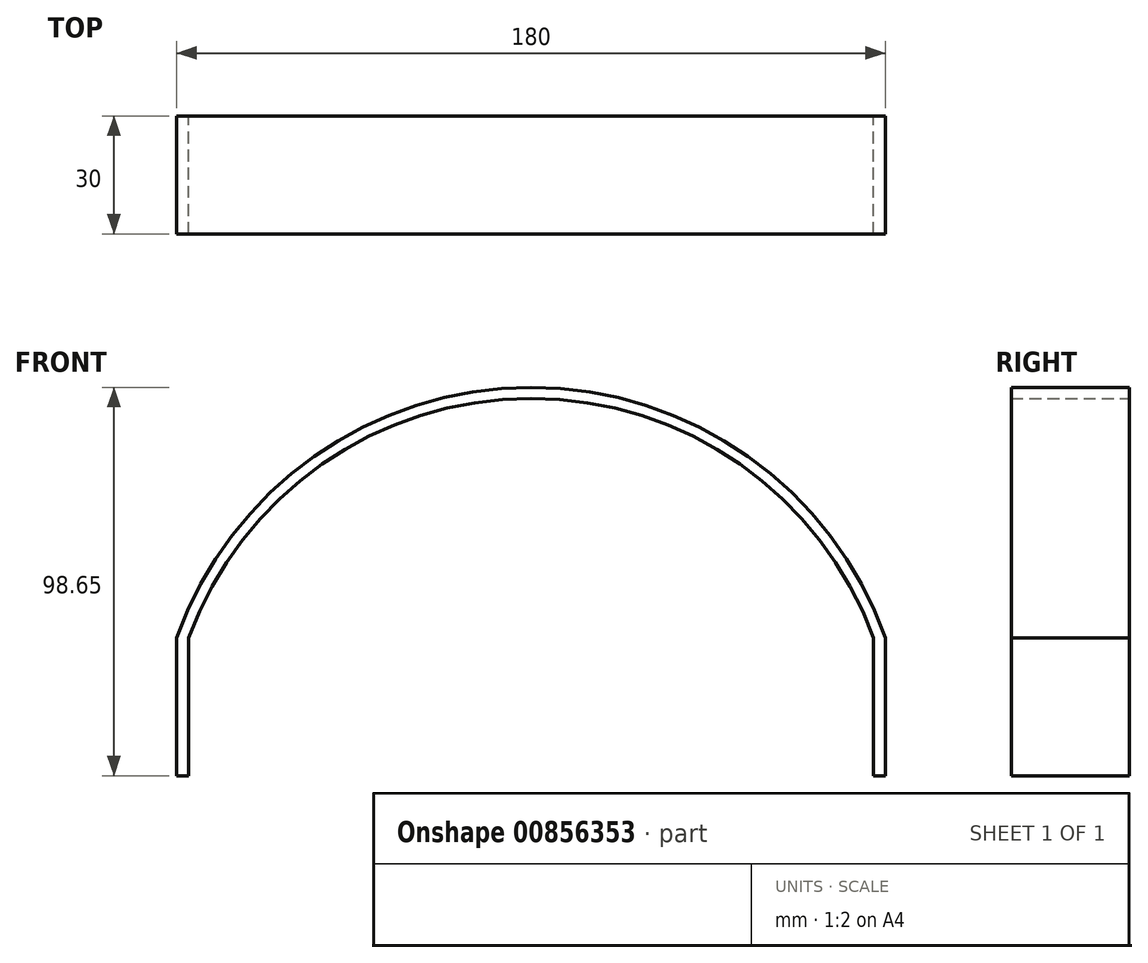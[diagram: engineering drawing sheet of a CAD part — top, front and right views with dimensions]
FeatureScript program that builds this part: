
annotation { "Feature Type Name" : "Feature", "Feature Type Description" : "" }
export const myFeature = defineFeature(function(context is Context, id is Id, definition is map)
    precondition{}
    {
        {
            var Q0;
            Q0=qCreatedBy(makeId("Front.planeOp"),FACE);
            var sketch = newSketch(context, id + "F0", { "sketchPlane" : qUnion([Q0])});
            skArc(sketch, "E0", {"start": v(95, 0) * mm, "mid": v(5, 63.65) * mm, "end": v(-85, 0) * mm});
            skLineSegment(sketch, "E1", {"start": v(-85, 0) * mm, "end": v(-85, -35) * mm});
            skLineSegment(sketch, "E2", {"start": v(-85, -35) * mm, "end": v(-82, -35) * mm});
            skLineSegment(sketch, "E3", {"start": v(-82, -35) * mm, "end": v(-82, 0) * mm});
            skLineSegment(sketch, "E4", {"start": v(95, 0) * mm, "end": v(95, -35) * mm});
            skLineSegment(sketch, "E5", {"start": v(95, -35) * mm, "end": v(92, -35) * mm});
            skLineSegment(sketch, "E6", {"start": v(92, -35) * mm, "end": v(92, 0) * mm});
            skArc(sketch, "E7", {"start": v(92, 0) * mm, "mid": v(5, 60.86) * mm, "end": v(-82, 0) * mm});
            skSolve(sketch);
        }
        {
            var Q0;
            Q0=makeQuery(id+"F0.imprint","IMPRINT",FACE,{"disambiguationData":[TD([[makeQuery(id+"F0.imprint","IMPRINT",EDGE,{"derivedFrom":sQuery(id+"F0.wireOp",EDGE,"E0")}),1.0]])]});
            extrude(context, id + "F1", {"entities" : qUnion([Q0]), "depth" : 30 * mm, "offsetDistance" : 25 * mm});
        }
    });
